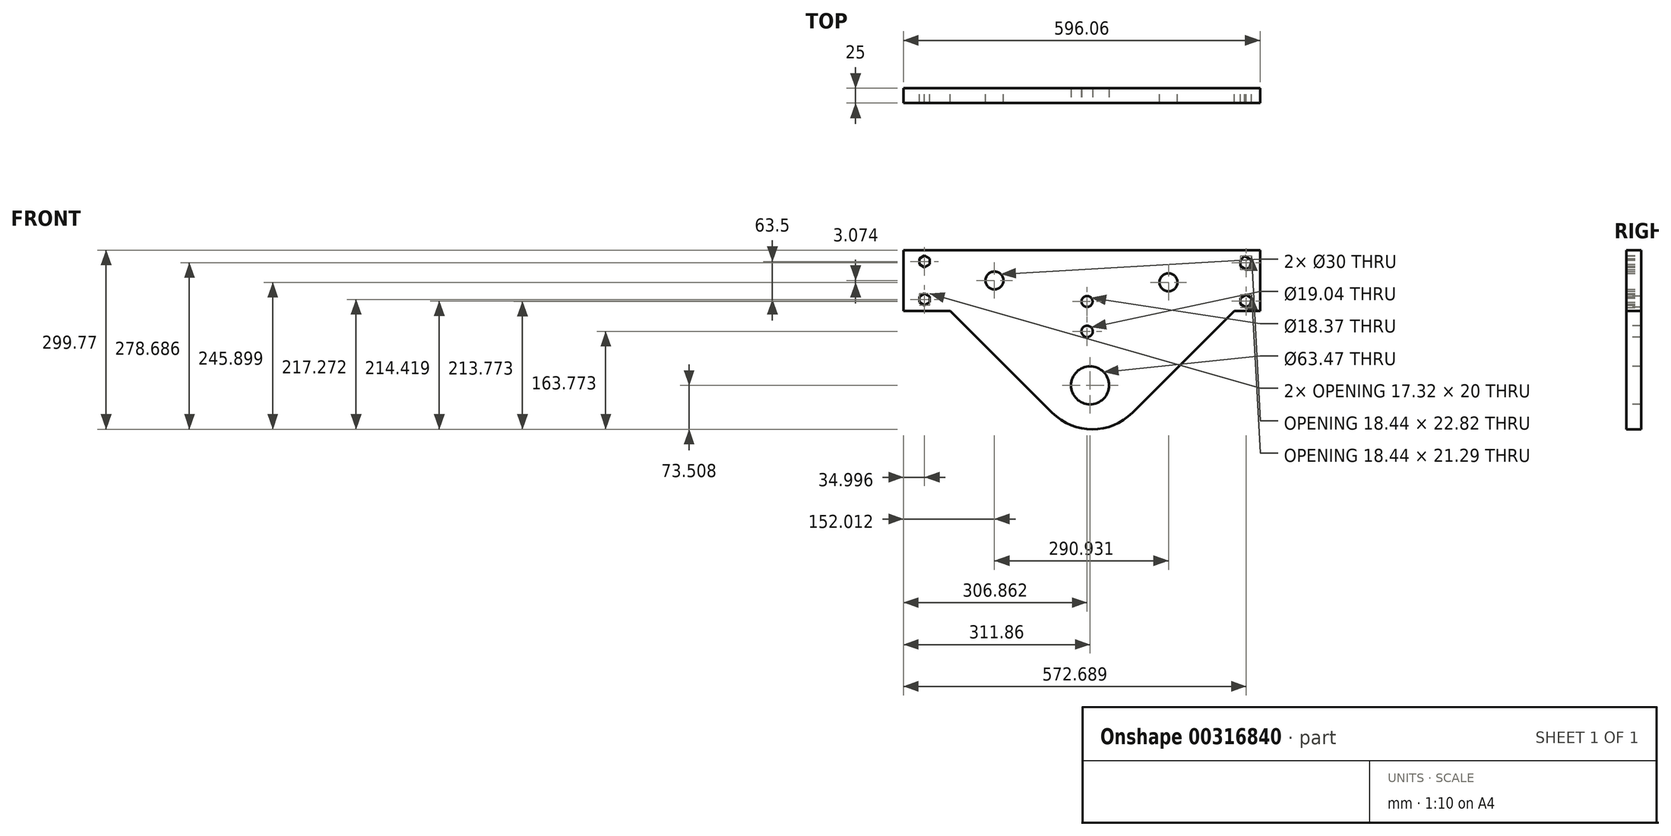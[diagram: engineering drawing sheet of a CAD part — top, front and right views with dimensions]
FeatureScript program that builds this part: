
annotation { "Feature Type Name" : "Feature", "Feature Type Description" : "" }
export const myFeature = defineFeature(function(context is Context, id is Id, definition is map)
    precondition{}
    {
        {
            var Q0;
            Q0=qCreatedBy(makeId("Front.planeOp"),FACE);
            var sketch = newSketch(context, id + "F0", { "sketchPlane" : qUnion([Q0])});
            skLineSegment(sketch, "E0.bottom", {"start": v(-311.86, 65.3) * mm, "end": v(-31.86, 65.3) * mm});
            skLineSegment(sketch, "E0.top", {"start": v(-311.86, -36.3) * mm, "end": v(-31.86, -36.3) * mm});
            skLineSegment(sketch, "E0.left", {"start": v(-311.86, 65.3) * mm, "end": v(-311.86, -36.3) * mm});
            skLineSegment(sketch, "E0.right", {"start": v(284.2, 65.3) * mm, "end": v(284.2, -36.3) * mm});
            skLineSegment(sketch, "E1", {"start": v(4.2, 65.3) * mm, "end": v(4.2, -36.3) * mm});
            skLineSegment(sketch, "E2", {"start": v(-31.86, 65.3) * mm, "end": v(-31.86, -36.3) * mm});
            skLineSegment(sketch, "E3.trimOffspring", {"start": v(4.2, 65.3) * mm, "end": v(284.2, 65.3) * mm});
            skLineSegment(sketch, "E4.trimOffspring", {"start": v(4.2, -36.3) * mm, "end": v(284.2, -36.3) * mm});
            skCircle(sketch, "E5.cCircle", {"center": v(-276.86, 46.3) * mm, "radius": 8.66 * mm, "construction": true});
            skLineSegment(sketch, "E5.0", {"start": v(-268.2, 51.3) * mm, "end": v(-268.2, 41.3) * mm});
            skLineSegment(sketch, "E5.1", {"start": v(-268.2, 41.3) * mm, "end": v(-276.86, 36.3) * mm});
            skLineSegment(sketch, "E5.2", {"start": v(-276.86, 36.3) * mm, "end": v(-285.52, 41.3) * mm});
            skLineSegment(sketch, "E5.3", {"start": v(-285.52, 41.3) * mm, "end": v(-285.52, 51.3) * mm});
            skLineSegment(sketch, "E5.4", {"start": v(-285.52, 51.3) * mm, "end": v(-276.86, 56.3) * mm});
            skLineSegment(sketch, "E5.5", {"start": v(-276.86, 56.3) * mm, "end": v(-268.2, 51.3) * mm});
            skPoint(sketch, "E5.0.midPoint", {"position": v(-268.2, 46.3) * mm});
            skCircle(sketch, "E6.cCircle", {"center": v(-276.86, -17.2) * mm, "radius": 8.66 * mm, "construction": true});
            skLineSegment(sketch, "E6.0", {"start": v(-268.2, -12.2) * mm, "end": v(-268.2, -22.2) * mm});
            skLineSegment(sketch, "E6.1", {"start": v(-268.2, -22.2) * mm, "end": v(-276.86, -27.2) * mm});
            skLineSegment(sketch, "E6.2", {"start": v(-276.86, -27.2) * mm, "end": v(-285.52, -22.2) * mm});
            skLineSegment(sketch, "E6.3", {"start": v(-285.52, -22.2) * mm, "end": v(-285.52, -12.2) * mm});
            skLineSegment(sketch, "E6.4", {"start": v(-285.52, -12.2) * mm, "end": v(-276.86, -7.2) * mm});
            skLineSegment(sketch, "E6.5", {"start": v(-276.86, -7.2) * mm, "end": v(-268.2, -12.2) * mm});
            skPoint(sketch, "E6.0.midPoint", {"position": v(-268.2, -17.2) * mm});
            skLineSegment(sketch, "E7.MirrorCS", {"start": v(251.61, 48.76) * mm, "end": v(251.61, 38.12) * mm});
            skLineSegment(sketch, "E8.MirrorCS", {"start": v(270.05, 38.12) * mm, "end": v(270.05, 48.76) * mm});
            skPoint(sketch, "E9.MirrorP", {"position": v(251.61, 44.67) * mm});
            skLineSegment(sketch, "E10.MirrorCS", {"start": v(260.83, 32.8) * mm, "end": v(270.05, 38.12) * mm});
            skLineSegment(sketch, "E11.MirrorCS", {"start": v(251.61, 38.12) * mm, "end": v(260.83, 32.8) * mm});
            skCircle(sketch, "E12.MirrorC", {"center": v(254.56, 46.3) * mm, "radius": 9.22 * mm, "construction": true});
            skLineSegment(sketch, "E13.MirrorCS", {"start": v(258.17, 55.62) * mm, "end": v(251.61, 48.76) * mm});
            skLineSegment(sketch, "E14.MirrorCS", {"start": v(270.05, 48.76) * mm, "end": v(258.17, 55.62) * mm});
            skLineSegment(sketch, "E15.MirrorCS", {"start": v(270.05, -25.38) * mm, "end": v(270.05, -14.74) * mm});
            skLineSegment(sketch, "E16.MirrorCS", {"start": v(251.61, -14.74) * mm, "end": v(251.61, -25.38) * mm});
            skCircle(sketch, "E17.MirrorC", {"center": v(254.56, -17.2) * mm, "radius": 9.22 * mm, "construction": true});
            skPoint(sketch, "E18.MirrorP", {"position": v(252.2, -13.52) * mm});
            skLineSegment(sketch, "E19.MirrorCS", {"start": v(251.61, -25.38) * mm, "end": v(260.83, -30.7) * mm});
            skLineSegment(sketch, "E20.MirrorCS", {"start": v(260.83, -9.42) * mm, "end": v(251.61, -14.74) * mm});
            skLineSegment(sketch, "E21.MirrorCS", {"start": v(270.05, -14.74) * mm, "end": v(260.83, -9.42) * mm});
            skLineSegment(sketch, "E22.MirrorCS", {"start": v(260.83, -30.7) * mm, "end": v(270.05, -25.38) * mm});
            skLineSegment(sketch, "E23", {"start": v(-233.73, -36.3) * mm, "end": v(-63.32, -206.72) * mm});
            skLineSegment(sketch, "E24", {"start": v(241.14, -36.3) * mm, "end": v(70.73, -206.72) * mm});
            skArc(sketch, "E25", {"start": v(-63.32, -206.72) * mm, "mid": v(3.7, -234.48) * mm, "end": v(70.73, -206.72) * mm});
            skLineSegment(sketch, "E26", {"start": v(-31.86, 65.3) * mm, "end": v(4.2, 65.3) * mm});
            skLineSegment(sketch, "E27", {"start": v(-31.86, -36.3) * mm, "end": v(4.2, -36.3) * mm});
            skCircle(sketch, "E28", {"center": v(-159.85, 14.5) * mm, "radius": 15 * mm});
            skLineSegment(sketch, "E29", {"start": v(-13.83, 65.3) * mm, "end": v(-17.1, -244.83) * mm, "construction": true});
            skCircle(sketch, "E30.MirrorC", {"center": v(131.08, 11.42) * mm, "radius": 15 * mm});
            skSolve(sketch);
        }
        {
            var Q0;
            Q0=makeQuery(id+"F0.imprint","IMPRINT",FACE,{"disambiguationData":[TD([[makeQuery(id+"F0.imprint","IMPRINT",EDGE,{"derivedFrom":sQuery(id+"F0.wireOp",EDGE,"E0.bottom")}),-1.0]])]});
            var Q1;
            {var subQ3=sQuery(id+"F0.wireOp",EDGE,"E23");Q1=makeQuery(id+"F0.imprint","IMPRINT",FACE,{"disambiguationData":[TD([[makeQuery(id+"F0.imprint","IMPRINT",EDGE,{"derivedFrom":subQ3}),1.0]])]});}
            var Q2;
            {var subQ1=sQuery(id+"F0.wireOp",EDGE,"E0.right");Q2=makeQuery(id+"F0.imprint","IMPRINT",FACE,{"disambiguationData":[TD([[makeQuery(id+"F0.imprint","IMPRINT",EDGE,{"derivedFrom":subQ1}),-1.0]])]});}
            var Q3;
            Q3=makeQuery(id+"F0.imprint","IMPRINT",FACE,{"disambiguationData":[TD([[makeQuery(id+"F0.imprint","IMPRINT",EDGE,{"derivedFrom":sQuery(id+"F0.wireOp",EDGE,"E1")}),-1.0]])]});
            extrude(context, id + "F1", {"entities" : qUnion([Q0, Q1, Q2, Q3]), "depth" : 25 * mm});
        }
        {
            var Q0;
            Q0=makeQuery(id+"F1.opExtrude","CAP_FACE",FACE,{"disambiguationData":[OSD([sQuery(id+"F0.wireOp",EDGE,"E0.bottom"),sQuery(id+"F0.wireOp",EDGE,"E0.top"),sQuery(id+"F0.wireOp",EDGE,"E0.left"),sQuery(id+"F0.wireOp",EDGE,"E0.right"),sQuery(id+"F0.wireOp",EDGE,"E3.trimOffspring"),sQuery(id+"F0.wireOp",EDGE,"E4.trimOffspring"),sQuery(id+"F0.wireOp",EDGE,"E5.0"),sQuery(id+"F0.wireOp",EDGE,"E5.1"),sQuery(id+"F0.wireOp",EDGE,"E5.2"),sQuery(id+"F0.wireOp",EDGE,"E5.3"),sQuery(id+"F0.wireOp",EDGE,"E5.4"),sQuery(id+"F0.wireOp",EDGE,"E5.5"),sQuery(id+"F0.wireOp",EDGE,"E6.0"),sQuery(id+"F0.wireOp",EDGE,"E6.1"),sQuery(id+"F0.wireOp",EDGE,"E6.2"),sQuery(id+"F0.wireOp",EDGE,"E6.3"),sQuery(id+"F0.wireOp",EDGE,"E6.4"),sQuery(id+"F0.wireOp",EDGE,"E6.5"),sQuery(id+"F0.wireOp",EDGE,"E7.MirrorCS"),sQuery(id+"F0.wireOp",EDGE,"E8.MirrorCS"),sQuery(id+"F0.wireOp",EDGE,"E10.MirrorCS"),sQuery(id+"F0.wireOp",EDGE,"E11.MirrorCS"),sQuery(id+"F0.wireOp",EDGE,"E13.MirrorCS"),sQuery(id+"F0.wireOp",EDGE,"E14.MirrorCS"),sQuery(id+"F0.wireOp",EDGE,"E15.MirrorCS"),sQuery(id+"F0.wireOp",EDGE,"E16.MirrorCS"),sQuery(id+"F0.wireOp",EDGE,"E19.MirrorCS"),sQuery(id+"F0.wireOp",EDGE,"E20.MirrorCS"),sQuery(id+"F0.wireOp",EDGE,"E21.MirrorCS"),sQuery(id+"F0.wireOp",EDGE,"E22.MirrorCS"),sQuery(id+"F0.wireOp",EDGE,"E23"),sQuery(id+"F0.wireOp",EDGE,"E24"),sQuery(id+"F0.wireOp",EDGE,"E25"),sQuery(id+"F0.wireOp",EDGE,"E26")])],"isStart":false});
            var sketch = newSketch(context, id + "F2", { "sketchPlane" : qUnion([Q0])});
            skCircle(sketch, "E31", {"center": v(0, -160.97) * mm, "radius": 31.74 * mm});
            skCircle(sketch, "E32", {"center": v(-5, -20.7) * mm, "radius": 9.18 * mm});
            skCircle(sketch, "E33", {"center": v(-5, -70.7) * mm, "radius": 9.52 * mm});
            skLineSegment(sketch, "E34", {"start": v(-5, -20.7) * mm, "end": v(-5, -70.7) * mm});
            skSolve(sketch);
        }
        {
            var Q0;
            Q0=makeQuery(id+"F2.imprint","IMPRINT",FACE,{"disambiguationData":[TD([[makeQuery(id+"F2.imprint","IMPRINT",EDGE,{"derivedFrom":sQuery(id+"F2.wireOp",EDGE,"E33")}),1.0]])]});
            var Q1;
            Q1=makeQuery(id+"F2.imprint","IMPRINT",FACE,{"disambiguationData":[TD([[makeQuery(id+"F2.imprint","IMPRINT",EDGE,{"derivedFrom":sQuery(id+"F2.wireOp",EDGE,"E32")}),1.0]])]});
            var Q2;
            Q2=makeQuery(id+"F2.imprint","IMPRINT",FACE,{"disambiguationData":[TD([[makeQuery(id+"F2.imprint","IMPRINT",EDGE,{"derivedFrom":sQuery(id+"F2.wireOp",EDGE,"E31")}),1.0]])]});
            extrude(context, id + "F3", {"entities" : qUnion([Q0, Q1, Q2]), "operationType" : NewBodyOperationType.REMOVE, "endBound" : BoundingType.SYMMETRIC, "oppositeDirection" : true, "depth" : 83 * mm});
        }
    });
